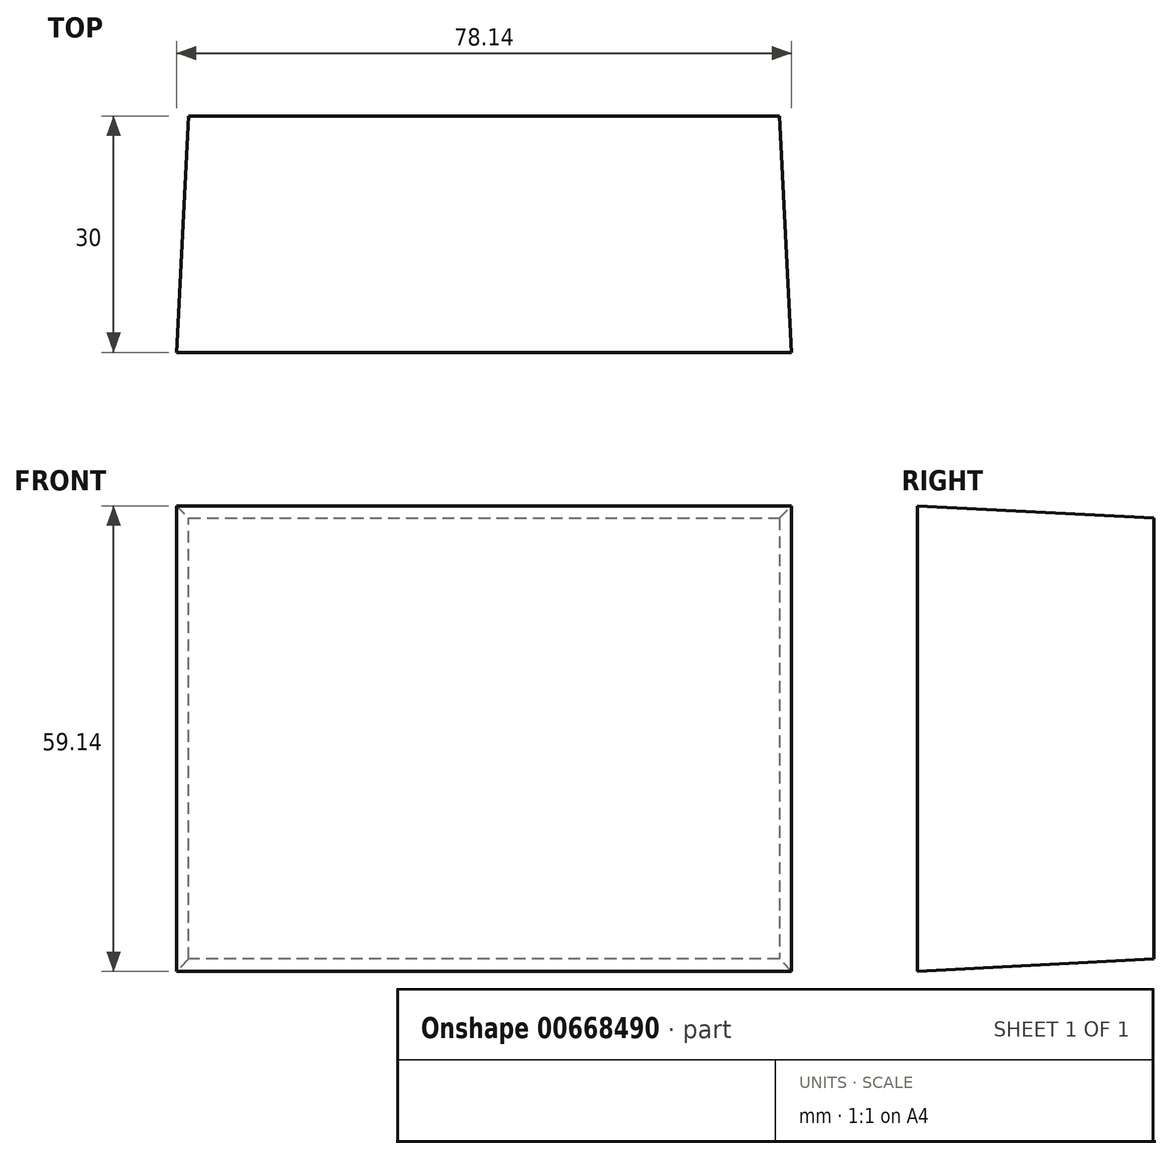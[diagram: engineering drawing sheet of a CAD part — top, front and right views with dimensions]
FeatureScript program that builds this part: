
annotation { "Feature Type Name" : "Feature", "Feature Type Description" : "" }
export const myFeature = defineFeature(function(context is Context, id is Id, definition is map)
    precondition{}
    {
        {
            var Q0;
            Q0=qCreatedBy(makeId("Front.planeOp"),FACE);
            var sketch = newSketch(context, id + "F0", { "sketchPlane" : qUnion([Q0])});
            skLineSegment(sketch, "E0.bottom", {"start": v(37.5, 28) * mm, "end": v(-37.5, 28) * mm});
            skLineSegment(sketch, "E0.top", {"start": v(37.5, -28) * mm, "end": v(-37.5, -28) * mm});
            skLineSegment(sketch, "E0.left", {"start": v(37.5, 28) * mm, "end": v(37.5, -28) * mm});
            skLineSegment(sketch, "E0.right", {"start": v(-37.5, 28) * mm, "end": v(-37.5, -28) * mm});
            skPoint(sketch, "E0.middle", {"position": v(0, 0) * mm});
            skSolve(sketch);
        }
        {
            var Q0;
            Q0=makeQuery(id+"F0.imprint","IMPRINT",FACE,{"disambiguationData":[TD([[makeQuery(id+"F0.imprint","IMPRINT",EDGE,{"derivedFrom":sQuery(id+"F0.wireOp",EDGE,"E0.bottom")}),1.0]])]});
            extrude(context, id + "F1", {"entities" : qUnion([Q0]), "depth" : 30 * mm, "offsetDistance" : 25 * mm, "hasDraft" : true, "draftAngle" : 3 * degree});
        }
    });
